# Revit family: Hager-Volta-IP30-Surface_mounted-sistema-ES-es
name_source: partatom
category: Electrical Equipment
units: mm (PartAtom-declared; Revit-internal decimal feet)

## family parameters
Cut with Voids When Loaded = No
Host = Face
Panel Configuration = Two Columns, Circuits Across
Part Type = Panelboard
Room Calculation Point = No
Round Connector Dimension = Use Diameter
Shared = No

## types (4) — shared parameters
EF000003 - Tipo de montaje = EV000384 - Montado superficial (escayola)
EF000007 - Color = EV000202 - Blanco
EF000008 - Anchura = 305 mm  [stored 1.00066 ft]
EF000049 - Profundidad = 96 mm  [stored 0.314961 ft]
EF000116 - Número RAL = 9010
EF000118 - Con placa de montaje = No
EF000339 - Tipo de cubierta = EV000494 - Ninguno
EF001062 - Versión de EMC = No
EF001088 - Posibilidad de extensión = Yes
EF001131 - Profundidad interna = 92 mm
EF001134 - Carril DIN = Yes
EF001596 - Material de la carcasa = EV000139 - Plástico
EF002950 - Anchura de unidades de división = 12
EF005474 - Grado de protección (IP) = EV006410 - IP30
EF006244 - Tapa/puerta transparente = No
EF006306 - Con cierre = No
EF009212 - Versión de la cubierta = EV009916 - Con muesca
EF015776 - Borne de tierra = Yes
EF015777 - Borne neutro = No
EF015941 - Puerta de transmisión de señal = No
HG000001 - Número de columnas = 1
HG000002 - Con puerta o tapa = No
HG000003 - Gama = Volta
HG000005 - Grosor = 3 mm  [stored 0.00984252 ft]
HG000006 - Empotrado = No
HG000009 - Puerta batiente doble = No
HG000010 - Puertas asimétricas = No
HG000011 - Filas vacías desde abajo = No
HG000017 - Distancia entre polos = 18 mm  [stored 0.0590551 ft]
Manufacturer = Hager
Type Comments = Volta
zero-valued in all types: Default Elevation, EF000218 - Profundidad de instalación, EF000332 - Altura de la instalación, EF000846 - Anchura de instalación, HG000007 - Número de columnas vacías, HG000008 - Número de filas vacías

## per-type parameters (varying)
| type | EF000040 - Altura | EF000266 - Número de filas | HG000004 - Referencia del fabricante | Model |
| Montado superficial IP30 A305 A245 P96.5 12 unidad de división - VA12E | 245 mm | 1 | VA12E | VA12E |
| Montado superficial IP30 A305 A370 P96.5 12 unidad de división - VA24E | 370 mm | 2 | VA24E | VA24E |
| Montado superficial IP30 A305 A515 P96.5 12 unidad de división - VA36E | 515 mm | 3 | VA36E | VA36E |
| Montado superficial IP30 A305 A640 P96.5 12 unidad de división - VA48E | 640 mm  [stored 2.09974 ft] | 4 | VA48E | VA48E |

note: [stored X ft] marks values corroborated as IEEE doubles in the binary element streams (Revit-internal decimal feet)

## geometry (parser evidence)
native form markers: Sweep x17
no freeform markers — native parametric forms only
